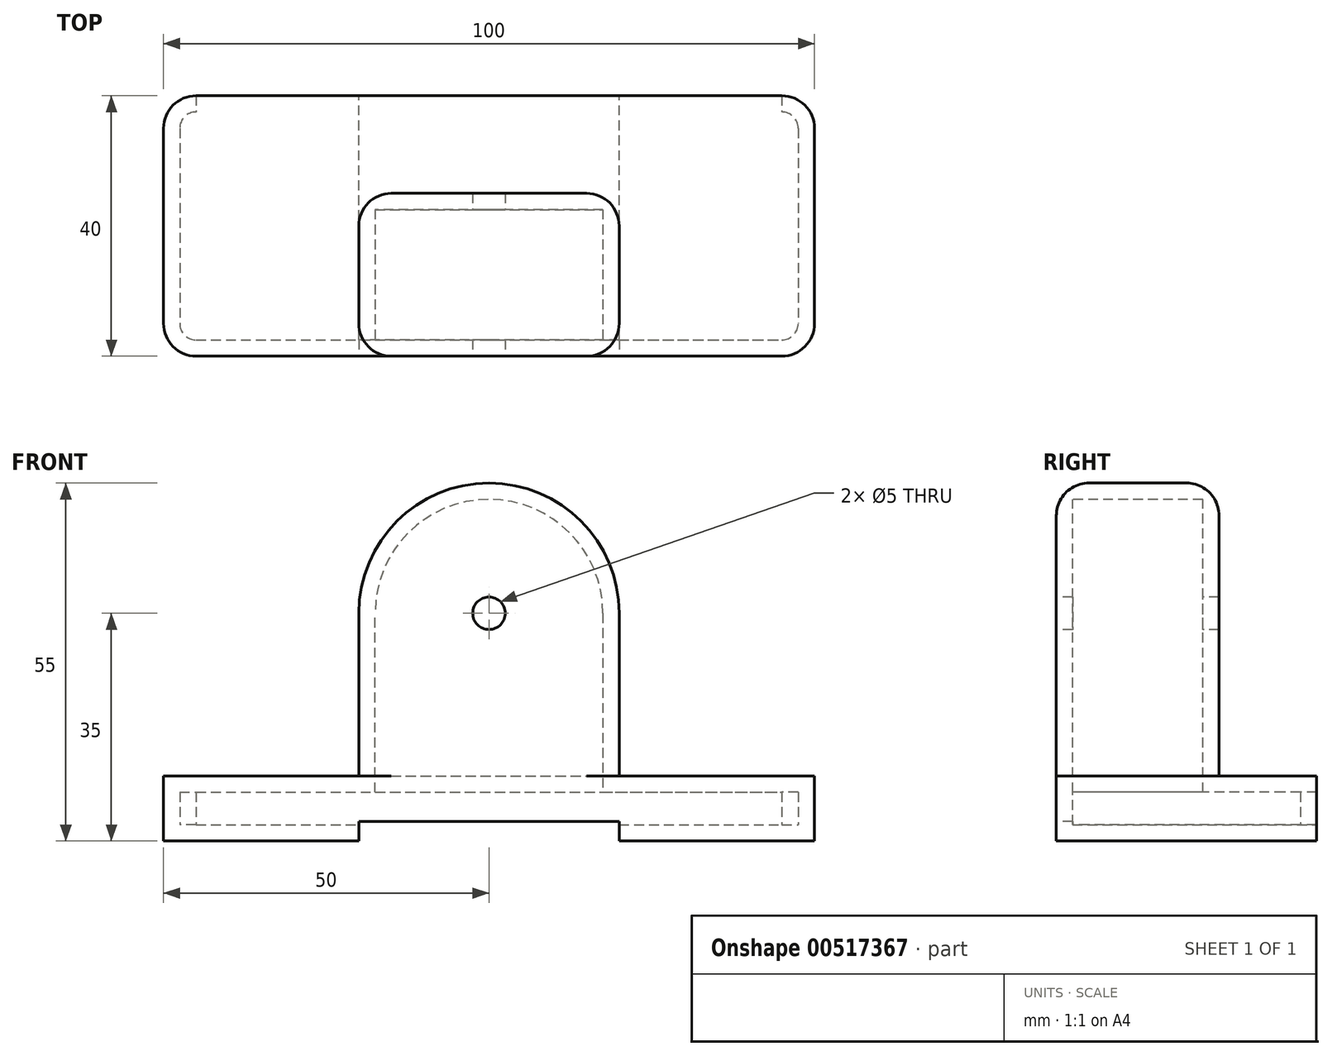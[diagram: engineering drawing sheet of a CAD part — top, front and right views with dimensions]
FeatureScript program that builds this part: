
annotation { "Feature Type Name" : "Feature", "Feature Type Description" : "" }
export const myFeature = defineFeature(function(context is Context, id is Id, definition is map)
    precondition{}
    {
        {
            var Q0;
            Q0=qCreatedBy(makeId("Top.planeOp"),FACE);
            var sketch = newSketch(context, id + "F0", { "sketchPlane" : qUnion([Q0])});
            skLineSegment(sketch, "E0.bottom", {"start": v(0, 0) * mm, "end": v(100, 0) * mm});
            skLineSegment(sketch, "E0.top", {"start": v(0, -40) * mm, "end": v(100, -40) * mm});
            skLineSegment(sketch, "E0.left", {"start": v(0, 0) * mm, "end": v(0, -40) * mm});
            skLineSegment(sketch, "E0.right", {"start": v(100, 0) * mm, "end": v(100, -40) * mm});
            skSolve(sketch);
        }
        {
            var Q0;
            Q0 = qSketchRegion(id + "F0", true);
            extrude(context, id + "F1", {"entities" : qUnion([Q0]), "depth" : 10 * mm, "offsetDistance" : 25 * mm});
        }
        {
            var Q0;
            Q0=makeQuery(id+"F1.opExtrude","SWEPT_FACE",FACE,{"disambiguationData":[OSD([sQuery(id+"F0.wireOp",EDGE,"E0.top")])]});
            var sketch = newSketch(context, id + "F2", { "sketchPlane" : qUnion([Q0])});
            skLineSegment(sketch, "E1", {"start": v(30, 0) * mm, "end": v(30, 35) * mm});
            skArc(sketch, "E2", {"start": v(70, 35) * mm, "mid": v(50, 55) * mm, "end": v(30, 35) * mm});
            skLineSegment(sketch, "E3", {"start": v(70, 35) * mm, "end": v(70, 0) * mm});
            skSolve(sketch);
        }
        {
            var Q0;
            Q0=makeQuery(id+"F1.opExtrude","SWEPT_EDGE",EDGE,{"disambiguationData":[OSD([sQuery(id+"F0.wireOp",EDGE,"E0.top"),sQuery(id+"F0.wireOp",EDGE,"E0.right")])]});
            fillet(context, id + "F3", {"entities" : qUnion([Q0]), "radius" : 5 * mm, "tangentPropagation" : true, "allowEdgeOverflow" : false});
        }
        {
            var Q0;
            Q0=makeQuery(id+"F1.opExtrude","SWEPT_EDGE",EDGE,{"disambiguationData":[OSD([sQuery(id+"F0.wireOp",EDGE,"E0.bottom"),sQuery(id+"F0.wireOp",EDGE,"E0.right")])]});
            fillet(context, id + "F4", {"entities" : qUnion([Q0]), "radius" : 5 * mm, "tangentPropagation" : true, "allowEdgeOverflow" : false});
        }
        {
            var Q0;
            Q0=makeQuery(id+"F1.opExtrude","SWEPT_EDGE",EDGE,{"disambiguationData":[OSD([sQuery(id+"F0.wireOp",EDGE,"E0.top"),sQuery(id+"F0.wireOp",EDGE,"E0.left")])]});
            fillet(context, id + "F5", {"entities" : qUnion([Q0]), "radius" : 5 * mm, "tangentPropagation" : true, "allowEdgeOverflow" : false});
        }
        {
            var Q0;
            Q0=makeQuery(id+"F1.opExtrude","SWEPT_EDGE",EDGE,{"disambiguationData":[OSD([sQuery(id+"F0.wireOp",EDGE,"E0.bottom"),sQuery(id+"F0.wireOp",EDGE,"E0.left")])]});
            fillet(context, id + "F6", {"entities" : qUnion([Q0]), "radius" : 5 * mm, "tangentPropagation" : true, "allowEdgeOverflow" : false});
        }
        {
            var Q0;
            {var subQ0=sQuery(id+"F2.wireOp",EDGE,"E2");Q0=makeQuery(id+"F2.imprint","IMPRINT",FACE,{"disambiguationData":[TD([[makeQuery(id+"F2.imprint","IMPRINT",EDGE,{"derivedFrom":subQ0}),1.0]])]});}
            var Q1;
            Q1=sQuery(id+"F2.wireOp",EDGE,"E2");
            extrude(context, id + "F7", {"entities" : qUnion([Q0]), "operationType" : NewBodyOperationType.ADD, "surfaceEntities" : qUnion([Q1]), "oppositeDirection" : true, "depth" : 25 * mm, "offsetDistance" : 25 * mm});
        }
        {
            var Q0;
            Q0=makeQuery(id+"F1.opExtrude","SWEPT_FACE",FACE,{"disambiguationData":[OSD([sQuery(id+"F0.wireOp",EDGE,"E0.bottom")])]});
            shell(context, id + "F8", {"entities" : qUnion([Q0]), "thickness" : 2.5 * mm});
        }
        {
            var Q0;
            Q0=makeQuery(id+"F7.opExtrude","CAP_EDGE",EDGE,{"disambiguationData":[OSD([sQuery(id+"F2.wireOp",EDGE,"E1")])],"isStart":true});
            fillet(context, id + "F9", {"entities" : qUnion([Q0]), "radius" : 5 * mm, "tangentPropagation" : true, "allowEdgeOverflow" : false});
        }
        {
            var Q0;
            Q0=makeQuery(id+"F7.opExtrude","CAP_EDGE",EDGE,{"disambiguationData":[OSD([sQuery(id+"F2.wireOp",EDGE,"E1")])],"isStart":false});
            fillet(context, id + "F10", {"entities" : qUnion([Q0]), "radius" : 5 * mm, "tangentPropagation" : true, "allowEdgeOverflow" : false});
        }
        {
            var Q0;
            {var subQ0=sQuery(id+"F0.wireOp",EDGE,"E0.top");Q0=makeQuery(id+"F7.boolean.opBoolean","MERGE",FACE,{"derivedFrom":[makeQuery(id+"F1.opExtrude","SWEPT_FACE",FACE,{"disambiguationData":[OSD([subQ0])]}),makeQuery(id+"F7.opExtrude","CAP_FACE",FACE,{"disambiguationData":[OSD([subQ0,sQuery(id+"F2.wireOp",EDGE,"E1"),sQuery(id+"F2.wireOp",EDGE,"E2"),sQuery(id+"F2.wireOp",EDGE,"E3")])],"isStart":true})]});}
            var sketch = newSketch(context, id + "F11", { "sketchPlane" : qUnion([Q0])});
            skCircle(sketch, "E4", {"center": v(50, 35) * mm, "radius": 6.12 * mm});
            skSolve(sketch);
        }
        {
            var Q0;
            Q0=sQuery(id+"F11.wireOp",VERTEX,"E4.center");
            var Q1;
            Q1=makeQuery(id+"F1.opExtrude","SWEPT_BODY",BODY,{"disambiguationData":[OSD([sQuery(id+"F0.wireOp",EDGE,"E0.bottom"),sQuery(id+"F0.wireOp",EDGE,"E0.top"),sQuery(id+"F0.wireOp",EDGE,"E0.left"),sQuery(id+"F0.wireOp",EDGE,"E0.right")])]});
            hole(context, id + "F12", {"style" : HoleStyle.SIMPLE, "endStyle" : HoleEndStyle.THROUGH, "holeDiameter" : 5 * mm, "isTappedThrough" : true, "tappedDepth" : 12 * mm, "tapClearance" : 3, "locations" : qUnion([Q0]), "scope" : qUnion([Q1])});
        }
        {
            var Q0;
            {var subQ0=sQuery(id+"F0.wireOp",EDGE,"E0.top");Q0=makeQuery(id+"F7.boolean.opBoolean","MERGE",FACE,{"derivedFrom":[makeQuery(id+"F1.opExtrude","SWEPT_FACE",FACE,{"disambiguationData":[OSD([subQ0])]}),makeQuery(id+"F7.opExtrude","CAP_FACE",FACE,{"disambiguationData":[OSD([subQ0,sQuery(id+"F2.wireOp",EDGE,"E1"),sQuery(id+"F2.wireOp",EDGE,"E2"),sQuery(id+"F2.wireOp",EDGE,"E3")])],"isStart":true})]});}
            var sketch = newSketch(context, id + "F13", { "sketchPlane" : qUnion([Q0])});
            skLineSegment(sketch, "E5.bottom", {"start": v(30, 0) * mm, "end": v(70, 0) * mm});
            skLineSegment(sketch, "E5.top", {"start": v(30, 3) * mm, "end": v(70, 3) * mm});
            skLineSegment(sketch, "E5.left", {"start": v(30, 0) * mm, "end": v(30, 3) * mm});
            skLineSegment(sketch, "E5.right", {"start": v(70, 0) * mm, "end": v(70, 3) * mm});
            skSolve(sketch);
        }
        {
            var Q0;
            Q0 = qSketchRegion(id + "F13", true);
            extrude(context, id + "F14", {"entities" : qUnion([Q0]), "operationType" : NewBodyOperationType.REMOVE, "endBound" : BoundingType.THROUGH_ALL, "oppositeDirection" : true, "depth" : 25 * mm, "offsetDistance" : 25 * mm});
        }
    });
